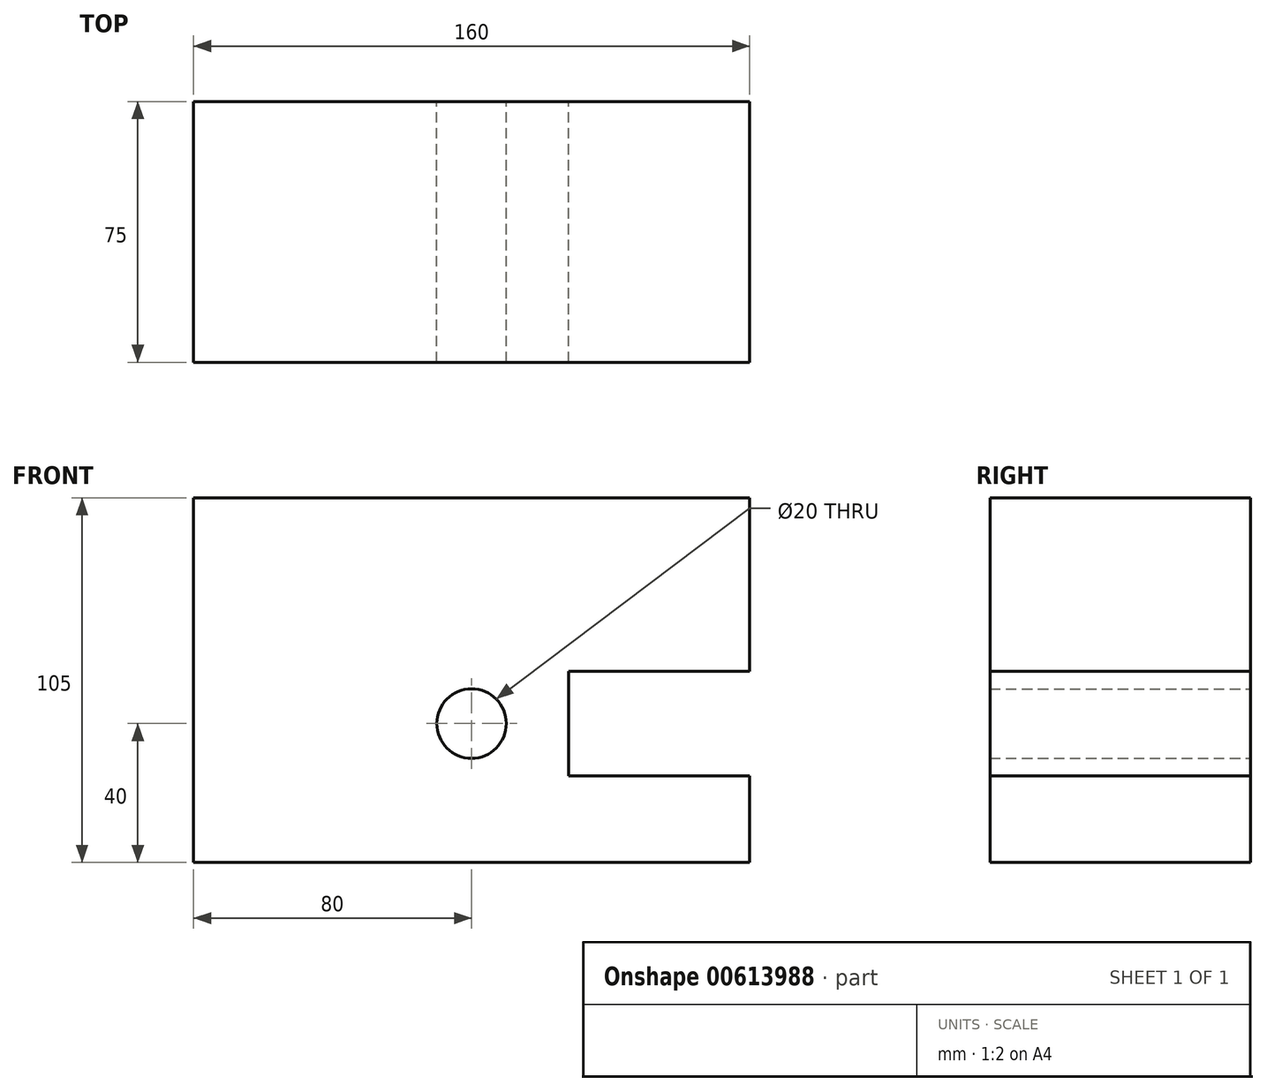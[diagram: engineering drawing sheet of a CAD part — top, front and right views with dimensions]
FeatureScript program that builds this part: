
annotation { "Feature Type Name" : "Feature", "Feature Type Description" : "" }
export const myFeature = defineFeature(function(context is Context, id is Id, definition is map)
    precondition{}
    {
        {
            var Q0;
            Q0=qCreatedBy(makeId("Front.planeOp"),FACE);
            var sketch = newSketch(context, id + "F0", { "sketchPlane" : qUnion([Q0])});
            skLineSegment(sketch, "E0.bottom", {"start": v(-80, 25) * mm, "end": v(80, 25) * mm});
            skLineSegment(sketch, "E0.top", {"start": v(-80, -55) * mm, "end": v(80, -55) * mm});
            skLineSegment(sketch, "E0.left", {"start": v(-80, 25) * mm, "end": v(-80, -55) * mm});
            skLineSegment(sketch, "E0.right", {"start": v(80, 25) * mm, "end": v(80, 0) * mm});
            skLineSegment(sketch, "E1", {"start": v(80, 0) * mm, "end": v(27.94, 0) * mm});
            skLineSegment(sketch, "E2", {"start": v(27.94, 0) * mm, "end": v(27.94, -30) * mm});
            skLineSegment(sketch, "E3", {"start": v(27.94, -30) * mm, "end": v(80, -30) * mm});
            skLineSegment(sketch, "E4.trimOffspring", {"start": v(80, -30) * mm, "end": v(80, -55) * mm});
            skLineSegment(sketch, "E5", {"start": v(17, 25) * mm, "end": v(17, -55) * mm});
            skLineSegment(sketch, "E6", {"start": v(-17, 25) * mm, "end": v(-17, -55) * mm});
            skLineSegment(sketch, "E7", {"start": v(27.94, -15) * mm, "end": v(-80, -15) * mm});
            skLineSegment(sketch, "E8", {"start": v(0, 25) * mm, "end": v(0, -55) * mm});
            skPoint(sketch, "E8.endSnap0", {"position": v(0, -55) * mm});
            skCircle(sketch, "E9", {"center": v(0, -15) * mm, "radius": 10 * mm});
            skSolve(sketch);
        }
        {
            var Q0;
            {var subQ0=sQuery(id+"F0.wireOp",EDGE,"E0.left");var subQ1=sQuery(id+"F0.wireOp",EDGE,"E0.bottom");var subQ2=makeQuery(id+"F0.imprint","INTERSECT",VERTEX,{"derivedFrom":[subQ1,subQ0]});Q0=makeQuery(id+"F0.imprint","IMPRINT",FACE,{"disambiguationData":[TD([[makeQuery(id+"F0.imprint","IMPRINT",EDGE,{"disambiguationData":[TD([[subQ2,-1.0]])],"derivedFrom":subQ1}),-1.0]])]});}
            var Q1;
            {var subQ4=sQuery(id+"F0.wireOp",EDGE,"E0.right");Q1=makeQuery(id+"F0.imprint","IMPRINT",FACE,{"disambiguationData":[TD([[makeQuery(id+"F0.imprint","IMPRINT",EDGE,{"derivedFrom":subQ4}),-1.0]])]});}
            var Q2;
            {var subQ1=sQuery(id+"F0.wireOp",EDGE,"E0.bottom");var subQ6=sQuery(id+"F0.wireOp",EDGE,"E5");var subQ9=makeQuery(id+"F0.imprint","INTERSECT",VERTEX,{"derivedFrom":[subQ1,subQ6]});Q2=makeQuery(id+"F0.imprint","IMPRINT",FACE,{"disambiguationData":[TD([[makeQuery(id+"F0.imprint","IMPRINT",EDGE,{"disambiguationData":[TD([[subQ9,1.0]])],"derivedFrom":subQ1}),-1.0]])]});}
            var Q3;
            {var subQ1=sQuery(id+"F0.wireOp",EDGE,"E6");var subQ5=sQuery(id+"F0.wireOp",EDGE,"E0.bottom");var subQ6=makeQuery(id+"F0.imprint","INTERSECT",VERTEX,{"derivedFrom":[subQ5,subQ1]});Q3=makeQuery(id+"F0.imprint","IMPRINT",FACE,{"disambiguationData":[TD([[makeQuery(id+"F0.imprint","IMPRINT",EDGE,{"disambiguationData":[TD([[subQ6,-1.0]])],"derivedFrom":subQ5}),-1.0]])]});}
            var Q4;
            {var subQ0=sQuery(id+"F0.wireOp",EDGE,"E0.left");var subQ1=sQuery(id+"F0.wireOp",EDGE,"E0.top");var subQ2=makeQuery(id+"F0.imprint","INTERSECT",VERTEX,{"derivedFrom":[subQ1,subQ0]});Q4=makeQuery(id+"F0.imprint","IMPRINT",FACE,{"disambiguationData":[TD([[makeQuery(id+"F0.imprint","IMPRINT",EDGE,{"disambiguationData":[TD([[subQ2,-1.0]])],"derivedFrom":subQ1}),1.0]])]});}
            var Q5;
            {var subQ1=sQuery(id+"F0.wireOp",EDGE,"E3");Q5=makeQuery(id+"F0.imprint","IMPRINT",FACE,{"disambiguationData":[TD([[makeQuery(id+"F0.imprint","IMPRINT",EDGE,{"derivedFrom":subQ1}),-1.0]])]});}
            var Q6;
            {var subQ1=sQuery(id+"F0.wireOp",EDGE,"E0.top");var subQ6=sQuery(id+"F0.wireOp",EDGE,"E6");var subQ9=makeQuery(id+"F0.imprint","INTERSECT",VERTEX,{"derivedFrom":[subQ1,subQ6]});Q6=makeQuery(id+"F0.imprint","IMPRINT",FACE,{"disambiguationData":[TD([[makeQuery(id+"F0.imprint","IMPRINT",EDGE,{"disambiguationData":[TD([[subQ9,-1.0]])],"derivedFrom":subQ1}),1.0]])]});}
            var Q7;
            {var subQ1=sQuery(id+"F0.wireOp",EDGE,"E0.top");var subQ5=sQuery(id+"F0.wireOp",EDGE,"E5");var subQ6=makeQuery(id+"F0.imprint","INTERSECT",VERTEX,{"derivedFrom":[subQ1,subQ5]});Q7=makeQuery(id+"F0.imprint","IMPRINT",FACE,{"disambiguationData":[TD([[makeQuery(id+"F0.imprint","IMPRINT",EDGE,{"disambiguationData":[TD([[subQ6,1.0]])],"derivedFrom":subQ1}),1.0]])]});}
            extrude(context, id + "F1", {"entities" : qUnion([Q0, Q1, Q2, Q3, Q4, Q5, Q6, Q7]), "depth" : 75 * mm, "offsetDistance" : 25 * mm});
        }
        {
            var Q0;
            Q0=makeQuery(id+"F1.opExtrude","SWEPT_FACE",FACE,{"disambiguationData":[OSD([sQuery(id+"F0.wireOp",EDGE,"E0.bottom")])]});
            extrude(context, id + "F2", {"entities" : qUnion([Q0]), "operationType" : NewBodyOperationType.ADD, "depth" : 25 * mm, "offsetDistance" : 25 * mm});
        }
    });
